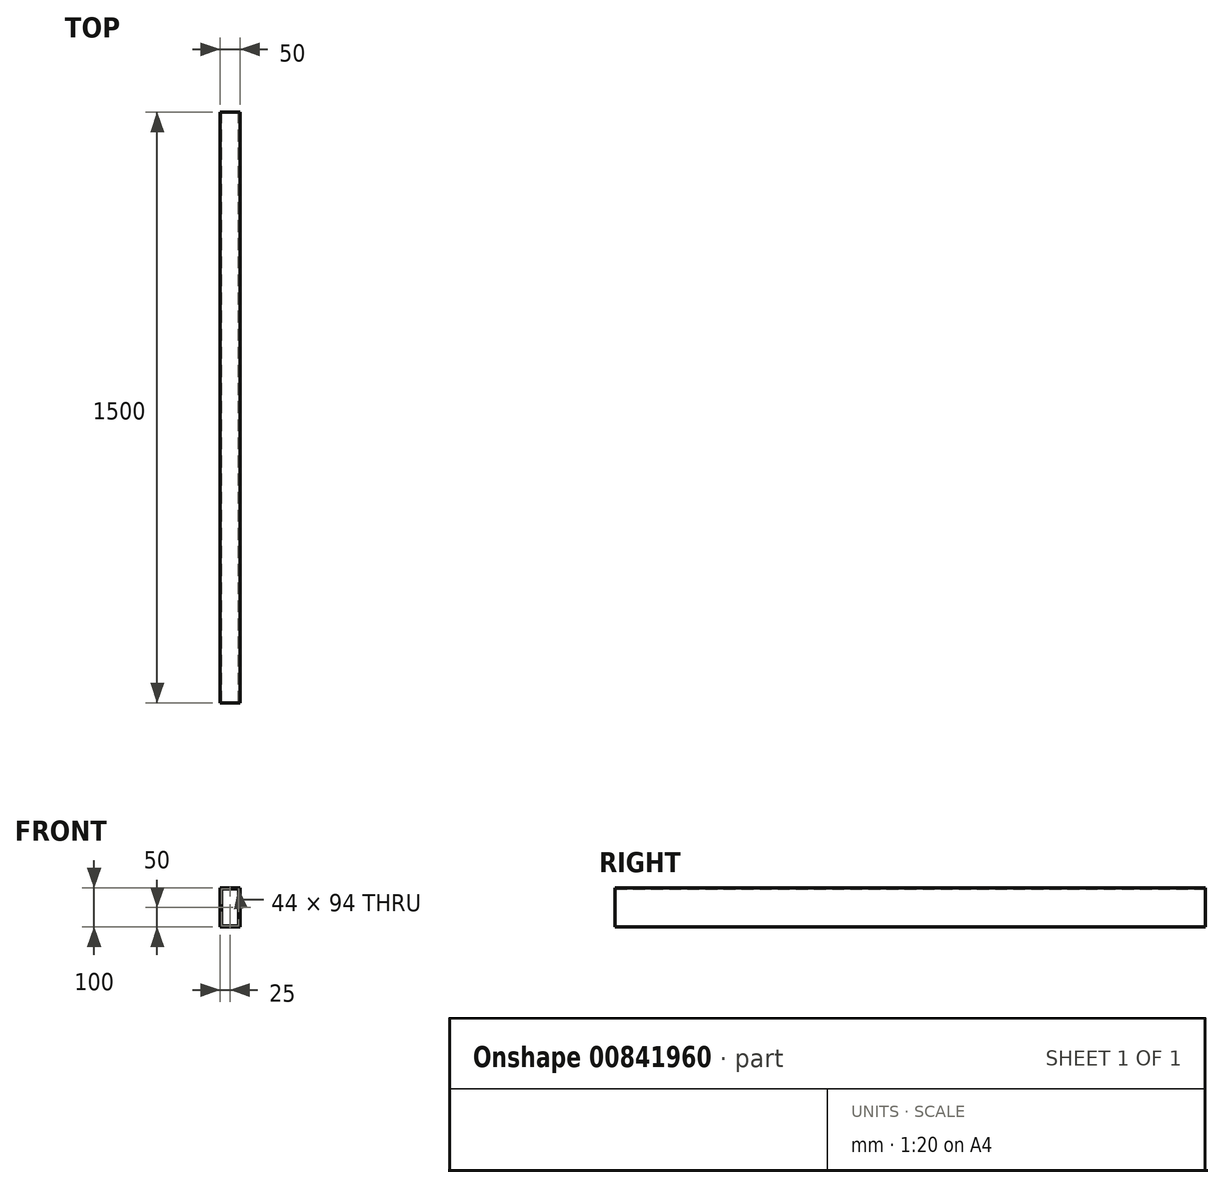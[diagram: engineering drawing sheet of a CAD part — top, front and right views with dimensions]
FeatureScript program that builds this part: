
annotation { "Feature Type Name" : "Feature", "Feature Type Description" : "" }
export const myFeature = defineFeature(function(context is Context, id is Id, definition is map)
    precondition{}
    {
        {
            var Q0;
            Q0=qCreatedBy(makeId("Front.planeOp"),FACE);
            var sketch = newSketch(context, id + "F0", { "sketchPlane" : qUnion([Q0])});
            skLineSegment(sketch, "E0.bottom", {"start": v(-25, 50) * mm, "end": v(25, 50) * mm});
            skLineSegment(sketch, "E0.top", {"start": v(-25, -50) * mm, "end": v(25, -50) * mm});
            skLineSegment(sketch, "E0.left", {"start": v(-25, 50) * mm, "end": v(-25, -50) * mm});
            skLineSegment(sketch, "E0.right", {"start": v(25, 50) * mm, "end": v(25, -50) * mm});
            skLineSegment(sketch, "E1.0", {"start": v(-22, 47) * mm, "end": v(-22, -47) * mm});
            skLineSegment(sketch, "E1.1", {"start": v(-22, 47) * mm, "end": v(22, 47) * mm});
            skLineSegment(sketch, "E1.2", {"start": v(22, 47) * mm, "end": v(22, -47) * mm});
            skLineSegment(sketch, "E1.3", {"start": v(-22, -47) * mm, "end": v(22, -47) * mm});
            skSolve(sketch);
        }
        {
            var Q0;
            Q0=makeQuery(id+"F0.imprint","IMPRINT",FACE,{"disambiguationData":[TD([[makeQuery(id+"F0.imprint","IMPRINT",EDGE,{"derivedFrom":sQuery(id+"F0.wireOp",EDGE,"E0.bottom")}),-1.0]])]});
            extrude(context, id + "F1", {"entities" : qUnion([Q0]), "endBound" : BoundingType.SYMMETRIC, "depth" : 1500 * mm, "offsetDistance" : 25 * mm});
        }
    });
